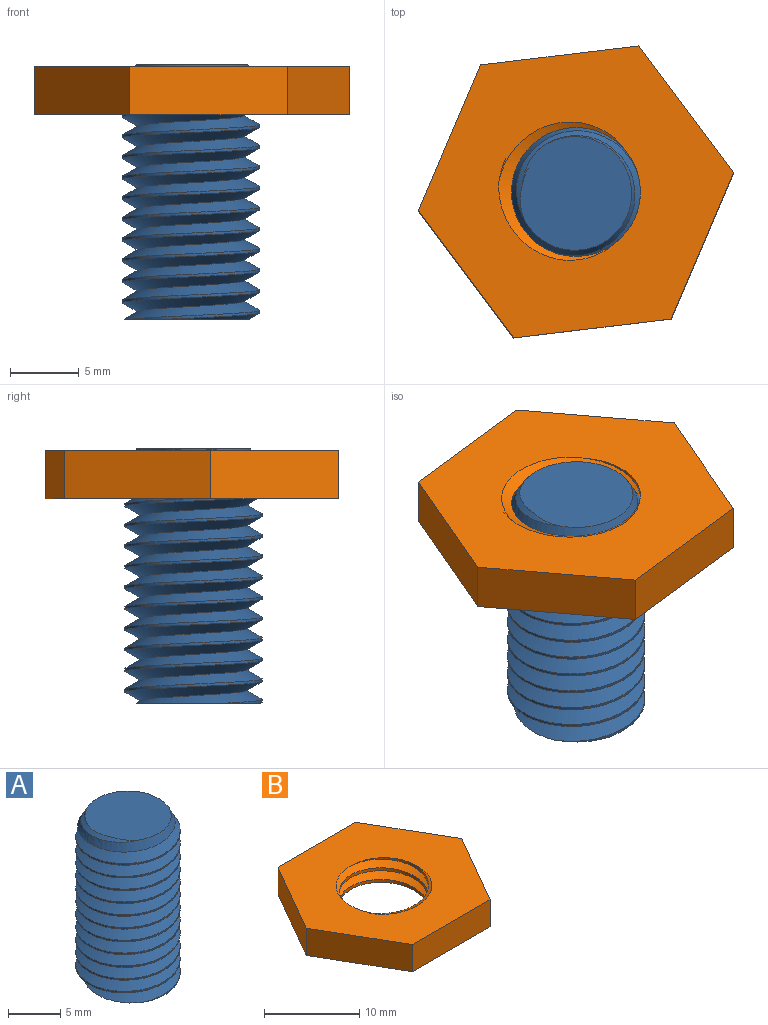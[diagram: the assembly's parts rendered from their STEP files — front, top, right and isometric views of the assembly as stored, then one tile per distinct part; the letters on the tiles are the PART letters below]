
ASSEMBLY  parts=2 mates=1
PART A: 6 faces, bbox 10.8x12.3x20.9 mm
  f0: cylinder r=5mm len=17mm, axis (0,0,-1), area 35mm2, adj f1,f2,f3,f5
  f1: bspline ~20.16x11.55mm, area 435.8mm2, adj f0,f2,f3,f4,f5
  f2: bspline ~19.66x11.55mm, area 434.5mm2, adj f0,f1,f3,f4,f5
  f3: plane 9.86x9.74mm, normal (0,0,-1), area 64.1mm2, adj f0,f1,f2
  f4: plane 8.31x8.23mm, normal (0,0,1), area 53mm2, adj f1,f2,f5
  f5: cone r=5mm half-angle=30deg, axis (0,0,-1), area 22.3mm2, adj f0,f1,f2,f4
PART B: 11 faces, bbox 23.7x20.6x5.5 mm
  f0: plane 10x5.77mm, normal (-0.87,0.5,0), area 40.4mm2, adj f1,f5,f9,f10
  f1: plane 10x5.77mm, normal (-0.87,-0.5,0), area 40.4mm2, adj f0,f2,f9,f10
  f2: plane 11.55x3.5mm, normal (0,-1,0), area 40.4mm2, adj f1,f3,f9,f10
  f3: plane 10x5.77mm, normal (0.87,-0.5,0), area 40.4mm2, adj f2,f4,f9,f10
  f4: plane 10x5.77mm, normal (0.87,0.5,0), area 40.4mm2, adj f3,f5,f9,f10
  f5: plane 11.55x3.5mm, normal (0,1,0), area 40.4mm2, adj f0,f4,f9,f10
  f6: cylinder r=4.69mm len=9.38mm, axis (0,0,-1), area 25.7mm2, adj f7,f8,f9,f10
  f7: bspline ~13.08x11.32mm, area 85.4mm2, adj f6,f8,f9,f10
  f8: bspline ~13.08x11.32mm, area 85.5mm2, adj f6,f7,f9,f10
  f9: plane 23.7x20.61mm, normal (0,0,-1), area 265.9mm2, adj f0,f1,f2,f3,f4,f5,f6,f7
  f10: plane 23.7x20.6mm, normal (0,0,1), area 265.9mm2, adj f0,f1,f2,f3,f4,f5,f6,f7
PLACE A rot(axis=(0,0,-1),33.2deg) t=(-19.57,27.7,-13)mm
PLACE B rot(axis=(0,0,-1),53.1deg) t=(-37.48,51.81,1.86)mm fixed
MATE cylindrical A.f0 <-> B.f9  axis (0,0,1) through (-19.57,27.7,-13)mm
